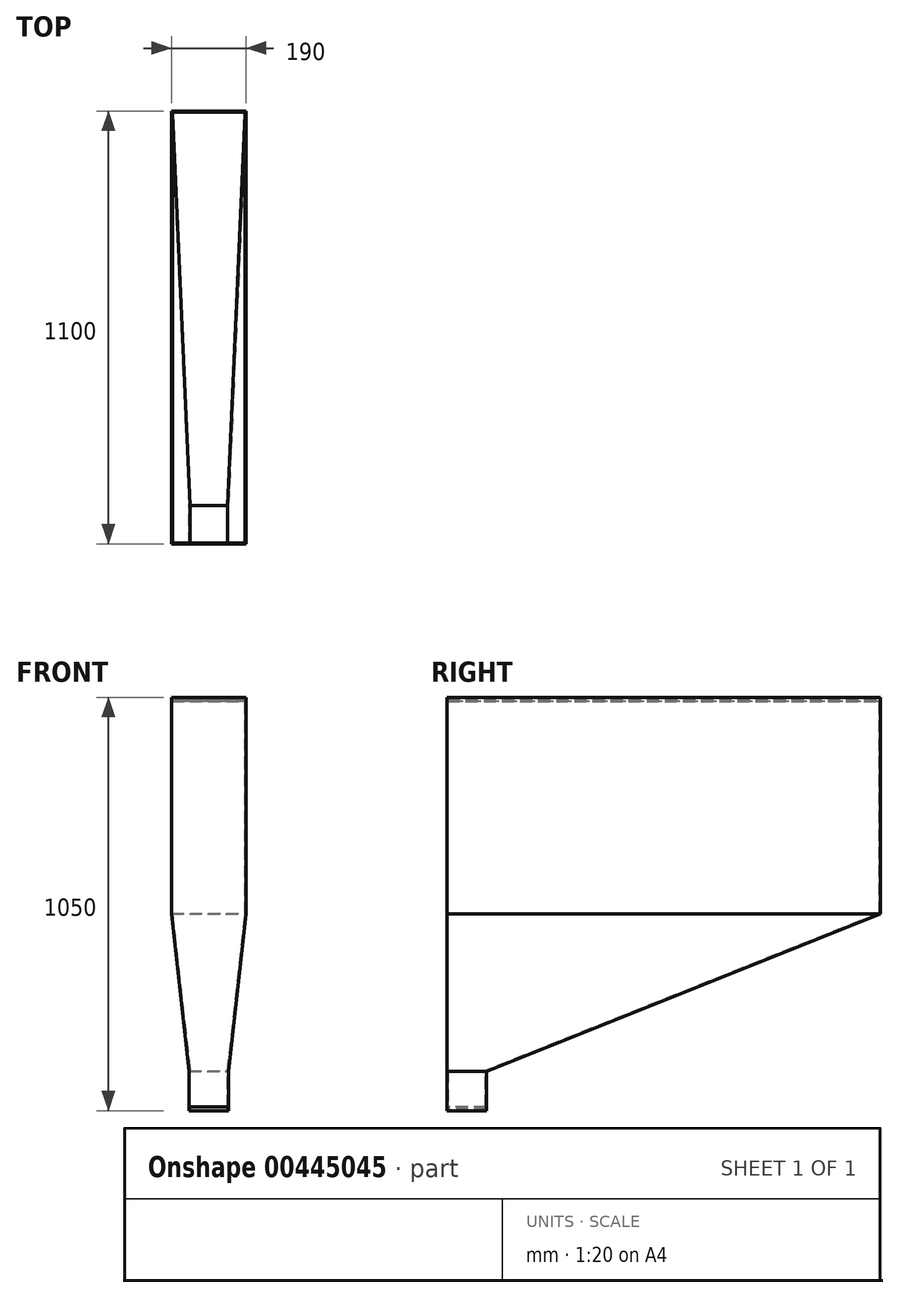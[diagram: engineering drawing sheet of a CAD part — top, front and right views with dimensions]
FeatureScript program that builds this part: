
annotation { "Feature Type Name" : "Feature", "Feature Type Description" : "" }
export const myFeature = defineFeature(function(context is Context, id is Id, definition is map)
    precondition{}
    {
        {
            var Q0;
            Q0=qCreatedBy(makeId("Front.planeOp"),FACE);
            var sketch = newSketch(context, id + "F0", { "sketchPlane" : qUnion([Q0])});
            skLineSegment(sketch, "E0.bottom", {"start": v(95, 0) * mm, "end": v(-95, 0) * mm});
            skLineSegment(sketch, "E0.top", {"start": v(95, 550) * mm, "end": v(-95, 550) * mm});
            skLineSegment(sketch, "E0.left", {"start": v(95, 0) * mm, "end": v(95, 550) * mm});
            skLineSegment(sketch, "E0.right", {"start": v(-95, 0) * mm, "end": v(-95, 550) * mm});
            skLineSegment(sketch, "E1.bottom", {"start": v(-50, -400) * mm, "end": v(50, -400) * mm});
            skLineSegment(sketch, "E1.top", {"start": v(-50, -500) * mm, "end": v(50, -500) * mm});
            skLineSegment(sketch, "E1.left", {"start": v(-50, -400) * mm, "end": v(-50, -500) * mm});
            skLineSegment(sketch, "E1.right", {"start": v(50, -400) * mm, "end": v(50, -500) * mm});
            skLineSegment(sketch, "E2", {"start": v(-50, -400) * mm, "end": v(-95, 0) * mm});
            skLineSegment(sketch, "E3", {"start": v(50, -400) * mm, "end": v(95, 0) * mm});
            skSolve(sketch);
        }
        {
            var Q0;
            Q0=makeQuery(id+"F0.imprint","IMPRINT",FACE,{"disambiguationData":[TD([[makeQuery(id+"F0.imprint","IMPRINT",EDGE,{"derivedFrom":sQuery(id+"F0.wireOp",EDGE,"E1.bottom")}),-1.0]])]});
            var Q1;
            Q1=makeQuery(id+"F0.imprint","IMPRINT",FACE,{"disambiguationData":[TD([[makeQuery(id+"F0.imprint","IMPRINT",EDGE,{"derivedFrom":sQuery(id+"F0.wireOp",EDGE,"E0.bottom")}),-1.0]])]});
            var Q2;
            Q2=makeQuery(id+"F0.imprint","IMPRINT",FACE,{"disambiguationData":[TD([[makeQuery(id+"F0.imprint","IMPRINT",EDGE,{"derivedFrom":sQuery(id+"F0.wireOp",EDGE,"E0.bottom")}),1.0]])]});
            extrude(context, id + "F1", {"entities" : qUnion([Q0, Q1, Q2]), "endBound" : BoundingType.SYMMETRIC, "depth" : 1100 * mm});
        }
        {
            var Q0;
            Q0=makeQuery(id+"F1.opExtrude","SWEPT_FACE",FACE,{"disambiguationData":[OSD([sQuery(id+"F0.wireOp",EDGE,"E0.left")])]});
            var sketch = newSketch(context, id + "F2", { "sketchPlane" : qUnion([Q0])});
            skLineSegment(sketch, "E4", {"start": v(550, 0) * mm, "end": v(550, -500) * mm});
            skLineSegment(sketch, "E5", {"start": v(550, -500) * mm, "end": v(-450, -500) * mm});
            skLineSegment(sketch, "E6", {"start": v(-450, -500) * mm, "end": v(-450, -400) * mm});
            skLineSegment(sketch, "E7", {"start": v(-450, -400) * mm, "end": v(550, 0) * mm});
            skSolve(sketch);
        }
        {
            var Q0;
            Q0=makeQuery(id+"F2.imprint","IMPRINT",FACE,{"disambiguationData":[TD([[makeQuery(id+"F2.imprint","IMPRINT",EDGE,{"derivedFrom":sQuery(id+"F2.wireOp",EDGE,"E4")}),-1.0]])]});
            extrude(context, id + "F3", {"entities" : qUnion([Q0]), "operationType" : NewBodyOperationType.REMOVE, "oppositeDirection" : true, "depth" : 190 * mm});
        }
        {
            var Q0;
            Q0=makeQuery(id+"F1.opExtrude","SWEPT_FACE",FACE,{"disambiguationData":[OSD([sQuery(id+"F0.wireOp",EDGE,"E0.top")])]});
            var Q1;
            Q1=makeQuery(id+"F1.opExtrude","SWEPT_FACE",FACE,{"disambiguationData":[OSD([sQuery(id+"F0.wireOp",EDGE,"E1.top")])]});
            shell(context, id + "F4", {"entities" : qUnion([Q0, Q1]), "thickness" : 2.5 * mm});
        }
        {
            var Q0;
            Q0=makeQuery(id+"F1.opExtrude","CAP_FACE",FACE,{"disambiguationData":[OSD([sQuery(id+"F0.wireOp",EDGE,"E0.top"),sQuery(id+"F0.wireOp",EDGE,"E0.left"),sQuery(id+"F0.wireOp",EDGE,"E0.right"),sQuery(id+"F0.wireOp",EDGE,"E1.top"),sQuery(id+"F0.wireOp",EDGE,"E1.left"),sQuery(id+"F0.wireOp",EDGE,"E1.right"),sQuery(id+"F0.wireOp",EDGE,"E2"),sQuery(id+"F0.wireOp",EDGE,"E3")])],"isStart":false});
            var sketch = newSketch(context, id + "F5", { "sketchPlane" : qUnion([Q0])});
            skLineSegment(sketch, "E8", {"start": v(-48.5, -500) * mm, "end": v(48.5, -500) * mm});
            skLineSegment(sketch, "E9", {"start": v(48.5, -500) * mm, "end": v(48.5, -495) * mm});
            skLineSegment(sketch, "E10", {"start": v(48.5, -495) * mm, "end": v(49.5, -495) * mm});
            skLineSegment(sketch, "E11", {"start": v(49.5, -495) * mm, "end": v(49.5, -490) * mm});
            skLineSegment(sketch, "E12", {"start": v(49.5, -490) * mm, "end": v(-49.5, -490) * mm});
            skLineSegment(sketch, "E13", {"start": v(-49.5, -490) * mm, "end": v(-49.5, -495) * mm});
            skLineSegment(sketch, "E14", {"start": v(-48.5, -500) * mm, "end": v(-48.5, -495) * mm});
            skLineSegment(sketch, "E15", {"start": v(-48.5, -495) * mm, "end": v(-49.5, -495) * mm});
            skSolve(sketch);
        }
        {
            var Q0;
            Q0=makeQuery(id+"F5.imprint","IMPRINT",FACE,{"disambiguationData":[TD([[makeQuery(id+"F5.imprint","IMPRINT",EDGE,{"derivedFrom":sQuery(id+"F5.wireOp",EDGE,"E8")}),1.0]])]});
            extrude(context, id + "F6", {"entities" : qUnion([Q0]), "operationType" : NewBodyOperationType.REMOVE, "oppositeDirection" : true, "depth" : 98.5 * mm});
        }
        {
            var Q0;
            Q0=makeQuery(id+"F1.opExtrude","CAP_FACE",FACE,{"disambiguationData":[OSD([sQuery(id+"F0.wireOp",EDGE,"E0.top"),sQuery(id+"F0.wireOp",EDGE,"E0.left"),sQuery(id+"F0.wireOp",EDGE,"E0.right"),sQuery(id+"F0.wireOp",EDGE,"E1.top"),sQuery(id+"F0.wireOp",EDGE,"E1.left"),sQuery(id+"F0.wireOp",EDGE,"E1.right"),sQuery(id+"F0.wireOp",EDGE,"E2"),sQuery(id+"F0.wireOp",EDGE,"E3")])],"isStart":true});
            var sketch = newSketch(context, id + "F7", { "sketchPlane" : qUnion([Q0])});
            skLineSegment(sketch, "E16.bottom", {"start": v(-92.5, 550) * mm, "end": v(92.5, 550) * mm});
            skLineSegment(sketch, "E16.top", {"start": v(-92.5, 545) * mm, "end": v(92.5, 545) * mm});
            skLineSegment(sketch, "E16.left", {"start": v(-92.5, 550) * mm, "end": v(-92.5, 545) * mm});
            skLineSegment(sketch, "E16.right", {"start": v(92.5, 550) * mm, "end": v(92.5, 545) * mm});
            skLineSegment(sketch, "E17.bottom", {"start": v(-94, 545) * mm, "end": v(94, 545) * mm});
            skLineSegment(sketch, "E17.top", {"start": v(-94, 540) * mm, "end": v(94, 540) * mm});
            skLineSegment(sketch, "E17.left", {"start": v(-94, 545) * mm, "end": v(-94, 540) * mm});
            skLineSegment(sketch, "E17.right", {"start": v(94, 545) * mm, "end": v(94, 540) * mm});
            skSolve(sketch);
        }
        {
            var Q0;
            Q0=makeQuery(id+"F7.imprint","IMPRINT",FACE,{"disambiguationData":[TD([[makeQuery(id+"F7.imprint","IMPRINT",EDGE,{"derivedFrom":sQuery(id+"F7.wireOp",EDGE,"E16.bottom")}),-1.0]])]});
            extrude(context, id + "F8", {"entities" : qUnion([Q0]), "operationType" : NewBodyOperationType.REMOVE, "oppositeDirection" : true, "depth" : 2.5 * mm});
        }
        {
            var Q0;
            Q0=makeQuery(id+"F7.imprint","IMPRINT",FACE,{"disambiguationData":[TD([[makeQuery(id+"F7.imprint","IMPRINT",EDGE,{"derivedFrom":sQuery(id+"F7.wireOp",EDGE,"E17.top")}),1.0]])]});
            extrude(context, id + "F9", {"entities" : qUnion([Q0]), "operationType" : NewBodyOperationType.REMOVE, "oppositeDirection" : true, "depth" : 1099 * mm});
        }
    });
